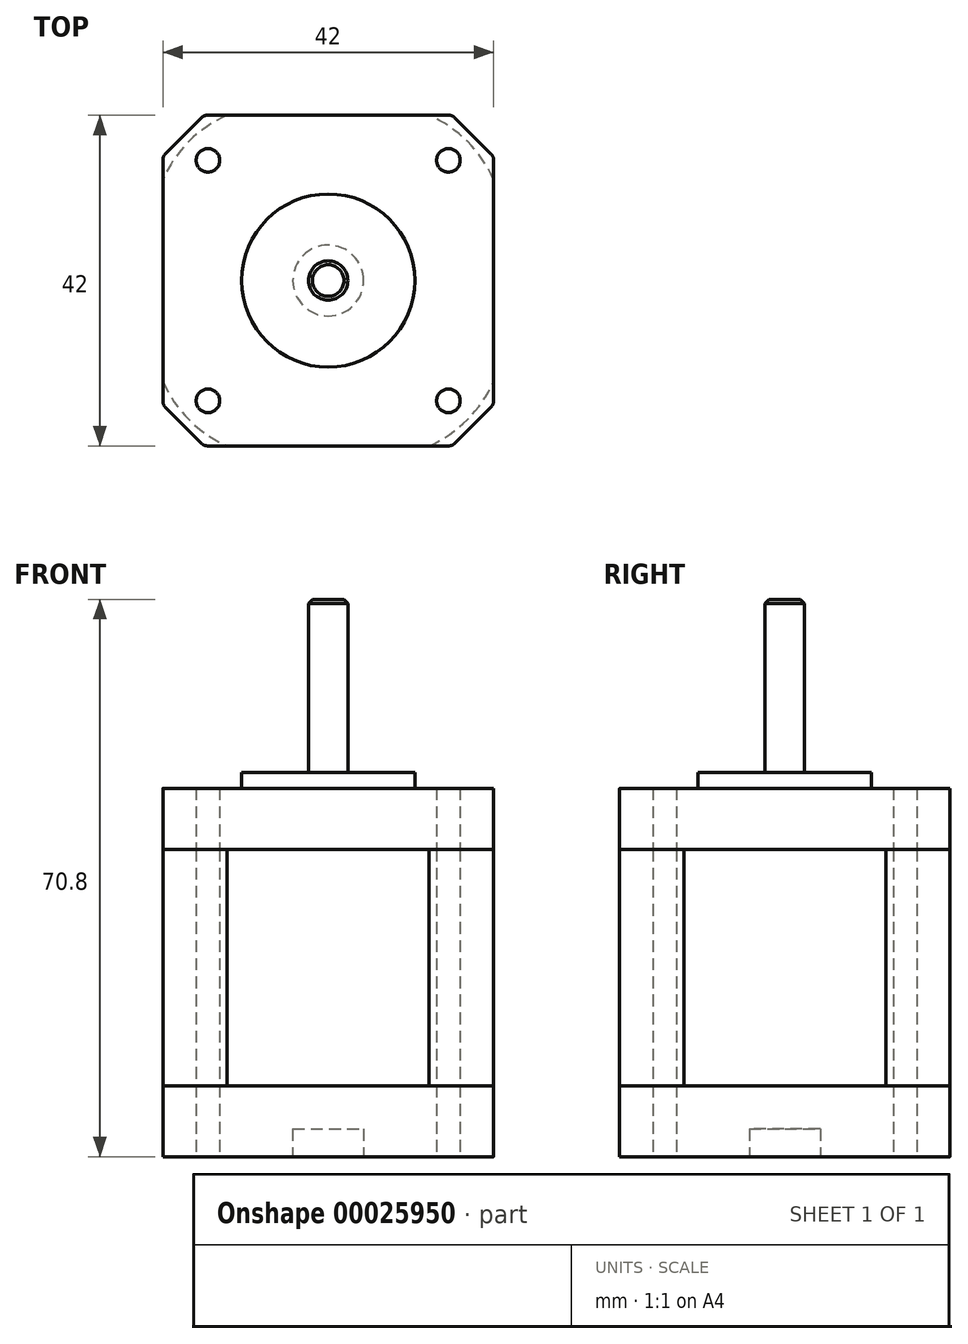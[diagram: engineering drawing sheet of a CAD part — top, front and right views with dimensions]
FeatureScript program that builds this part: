
annotation { "Feature Type Name" : "Feature", "Feature Type Description" : "" }
export const myFeature = defineFeature(function(context is Context, id is Id, definition is map)
    precondition{}
    {
        {
            var Q0;
            Q0=qCreatedBy(makeId("Top.planeOp"),FACE);
            var sketch = newSketch(context, id + "F0", { "sketchPlane" : qUnion([Q0])});
            skLineSegment(sketch, "E0.rect.bottom", {"start": v(-15.36, 21) * mm, "end": v(15.36, 21) * mm});
            skLineSegment(sketch, "E0.rect.top", {"start": v(-15.36, -21) * mm, "end": v(15.36, -21) * mm});
            skLineSegment(sketch, "E0.rect.left", {"start": v(-21, 15.36) * mm, "end": v(-21, -15.36) * mm});
            skLineSegment(sketch, "E0.rect.right", {"start": v(21, 15.36) * mm, "end": v(21, -15.36) * mm});
            skPoint(sketch, "E0.rect.middle", {"position": v(0, 0) * mm});
            skLineSegment(sketch, "E1", {"start": v(-20.7, 16.06) * mm, "end": v(-16.06, 20.7) * mm});
            skPoint(sketch, "E2.newPointA", {"position": v(-21, 21) * mm});
            skArc(sketch, "E2.filletArc", {"start": v(-20.7, 16.06) * mm, "mid": v(-20.92, 15.74) * mm, "end": v(-21, 15.36) * mm});
            skArc(sketch, "E3.filletArc", {"start": v(-15.36, 21) * mm, "mid": v(-15.74, 20.92) * mm, "end": v(-16.06, 20.7) * mm});
            skArc(sketch, "E4.1.0", {"start": v(-16.06, -20.7) * mm, "mid": v(-15.74, -20.92) * mm, "end": v(-15.36, -21) * mm});
            skLineSegment(sketch, "E4.1.1", {"start": v(-16.06, -20.7) * mm, "end": v(-20.7, -16.06) * mm});
            skArc(sketch, "E4.1.2", {"start": v(-21, -15.36) * mm, "mid": v(-20.92, -15.74) * mm, "end": v(-20.7, -16.06) * mm});
            skArc(sketch, "E4.2.0", {"start": v(20.7, -16.06) * mm, "mid": v(20.92, -15.74) * mm, "end": v(21, -15.36) * mm});
            skLineSegment(sketch, "E4.2.1", {"start": v(20.7, -16.06) * mm, "end": v(16.06, -20.7) * mm});
            skArc(sketch, "E4.2.2", {"start": v(15.36, -21) * mm, "mid": v(15.74, -20.92) * mm, "end": v(16.06, -20.7) * mm});
            skArc(sketch, "E4.3.0", {"start": v(16.06, 20.7) * mm, "mid": v(15.74, 20.92) * mm, "end": v(15.36, 21) * mm});
            skLineSegment(sketch, "E4.3.1", {"start": v(16.06, 20.7) * mm, "end": v(20.7, 16.06) * mm});
            skArc(sketch, "E4.3.2", {"start": v(21, 15.36) * mm, "mid": v(20.92, 15.74) * mm, "end": v(20.7, 16.06) * mm});
            skPoint(sketch, "E5.orphan", {"position": v(21, 21) * mm});
            skPoint(sketch, "E6.orphan", {"position": v(21, -21) * mm});
            skPoint(sketch, "E7.orphan", {"position": v(-21, -21) * mm});
            skSolve(sketch);
        }
        {
            var Q0;
            Q0=makeQuery(id+"F0.imprint","IMPRINT",FACE,{"disambiguationData":[TD([[makeQuery(id+"F0.imprint","IMPRINT",EDGE,{"derivedFrom":sQuery(id+"F0.wireOp",EDGE,"E0.rect.bottom")}),-1.0]])]});
            extrude(context, id + "F1", {"entities" : qUnion([Q0]), "depth" : 9 * mm});
        }
        {
            var Q0;
            Q0=makeQuery(id+"F1.opExtrude","CAP_FACE",FACE,{"disambiguationData":[OSD([sQuery(id+"F0.wireOp",EDGE,"E0.rect.bottom"),sQuery(id+"F0.wireOp",EDGE,"E0.rect.top"),sQuery(id+"F0.wireOp",EDGE,"E0.rect.left"),sQuery(id+"F0.wireOp",EDGE,"E0.rect.right"),sQuery(id+"F0.wireOp",EDGE,"E1"),sQuery(id+"F0.wireOp",EDGE,"E2.filletArc"),sQuery(id+"F0.wireOp",EDGE,"E3.filletArc"),sQuery(id+"F0.wireOp",EDGE,"E4.1.0"),sQuery(id+"F0.wireOp",EDGE,"E4.1.1"),sQuery(id+"F0.wireOp",EDGE,"E4.1.2"),sQuery(id+"F0.wireOp",EDGE,"E4.2.0"),sQuery(id+"F0.wireOp",EDGE,"E4.2.1"),sQuery(id+"F0.wireOp",EDGE,"E4.2.2"),sQuery(id+"F0.wireOp",EDGE,"E4.3.0"),sQuery(id+"F0.wireOp",EDGE,"E4.3.1"),sQuery(id+"F0.wireOp",EDGE,"E4.3.2")])],"isStart":false});
            var sketch = newSketch(context, id + "F2", { "sketchPlane" : qUnion([Q0])});
            skLineSegment(sketch, "E8.rect.bottom", {"start": v(-12.82, 21) * mm, "end": v(12.82, 21) * mm});
            skLineSegment(sketch, "E8.rect.top", {"start": v(-12.82, -21) * mm, "end": v(12.82, -21) * mm});
            skLineSegment(sketch, "E8.rect.left", {"start": v(-21, 12.82) * mm, "end": v(-21, -12.82) * mm});
            skLineSegment(sketch, "E8.rect.right", {"start": v(21, 12.82) * mm, "end": v(21, -12.82) * mm});
            skPoint(sketch, "E8.rect.middle", {"position": v(0, 0) * mm});
            skArc(sketch, "E9", {"start": v(-12.82, 21) * mm, "mid": v(-17.68, 17.68) * mm, "end": v(-21, 12.82) * mm});
            skPoint(sketch, "E10.orphan", {"position": v(-21, 0) * mm});
            skArc(sketch, "E11.1.0", {"start": v(-21, -12.82) * mm, "mid": v(-17.68, -17.68) * mm, "end": v(-12.82, -21) * mm});
            skArc(sketch, "E11.2.0", {"start": v(12.82, -21) * mm, "mid": v(17.68, -17.68) * mm, "end": v(21, -12.82) * mm});
            skArc(sketch, "E11.3.0", {"start": v(21, 12.82) * mm, "mid": v(17.68, 17.68) * mm, "end": v(12.82, 21) * mm});
            skPoint(sketch, "E12.orphan", {"position": v(-21, 21) * mm});
            skPoint(sketch, "E13.orphan", {"position": v(21, 21) * mm});
            skPoint(sketch, "E14.orphan", {"position": v(21, -21) * mm});
            skPoint(sketch, "E15.orphan", {"position": v(-21, -21) * mm});
            skSolve(sketch);
        }
        {
            var Q0;
            {var subQ3=sQuery(id+"F2.wireOp",EDGE,"E9");Q0=makeQuery(id+"F2.imprint","IMPRINT",FACE,{"disambiguationData":[TD([[makeQuery(id+"F2.imprint","IMPRINT",EDGE,{"derivedFrom":subQ3}),1.0]])]});}
            extrude(context, id + "F3", {"entities" : qUnion([Q0]), "depth" : 30 * mm});
        }
        {
            var Q0;
            Q0=makeQuery(id+"F3.opExtrude","CAP_FACE",FACE,{"disambiguationData":[OSD([sQuery(id+"F2.wireOp",EDGE,"E8.rect.bottom"),sQuery(id+"F2.wireOp",EDGE,"E8.rect.top"),sQuery(id+"F2.wireOp",EDGE,"E8.rect.left"),sQuery(id+"F2.wireOp",EDGE,"E8.rect.right"),sQuery(id+"F2.wireOp",EDGE,"E9"),sQuery(id+"F2.wireOp",EDGE,"E11.1.0"),sQuery(id+"F2.wireOp",EDGE,"E11.2.0"),sQuery(id+"F2.wireOp",EDGE,"E11.3.0")])],"isStart":false});
            var sketch = newSketch(context, id + "F4", { "sketchPlane" : qUnion([Q0])});
            skLineSegment(sketch, "E16.rect.bottom", {"start": v(-15.36, 21) * mm, "end": v(15.36, 21) * mm});
            skLineSegment(sketch, "E16.rect.top", {"start": v(-15.36, -21) * mm, "end": v(15.36, -21) * mm});
            skLineSegment(sketch, "E16.rect.left", {"start": v(-21, 15.36) * mm, "end": v(-21, -15.36) * mm});
            skLineSegment(sketch, "E16.rect.right", {"start": v(21, 15.36) * mm, "end": v(21, -15.36) * mm});
            skPoint(sketch, "E16.rect.middle", {"position": v(0, 0) * mm});
            skLineSegment(sketch, "E17", {"start": v(-20.7, 16.06) * mm, "end": v(-16.06, 20.7) * mm});
            skPoint(sketch, "E18.newPointA", {"position": v(-21, 37.25) * mm});
            skArc(sketch, "E18.filletArc", {"start": v(-20.7, 16.06) * mm, "mid": v(-20.92, 15.74) * mm, "end": v(-21, 15.36) * mm});
            skPoint(sketch, "E19.newPointA", {"position": v(-21, 21) * mm});
            skArc(sketch, "E19.filletArc", {"start": v(-15.36, 21) * mm, "mid": v(-15.74, 20.92) * mm, "end": v(-16.06, 20.7) * mm});
            skArc(sketch, "E20.1.0", {"start": v(-16.06, -20.7) * mm, "mid": v(-15.74, -20.92) * mm, "end": v(-15.36, -21) * mm});
            skLineSegment(sketch, "E20.1.1", {"start": v(-16.06, -20.7) * mm, "end": v(-20.7, -16.06) * mm});
            skArc(sketch, "E20.1.2", {"start": v(-21, -15.36) * mm, "mid": v(-20.92, -15.74) * mm, "end": v(-20.7, -16.06) * mm});
            skArc(sketch, "E20.2.0", {"start": v(20.7, -16.06) * mm, "mid": v(20.92, -15.74) * mm, "end": v(21, -15.36) * mm});
            skLineSegment(sketch, "E20.2.1", {"start": v(20.7, -16.06) * mm, "end": v(16.06, -20.7) * mm});
            skArc(sketch, "E20.2.2", {"start": v(15.36, -21) * mm, "mid": v(15.74, -20.92) * mm, "end": v(16.06, -20.7) * mm});
            skArc(sketch, "E20.3.0", {"start": v(16.06, 20.7) * mm, "mid": v(15.74, 20.92) * mm, "end": v(15.36, 21) * mm});
            skLineSegment(sketch, "E20.3.1", {"start": v(16.06, 20.7) * mm, "end": v(20.7, 16.06) * mm});
            skArc(sketch, "E20.3.2", {"start": v(21, 15.36) * mm, "mid": v(20.92, 15.74) * mm, "end": v(20.7, 16.06) * mm});
            skPoint(sketch, "E21.orphan", {"position": v(21, 21) * mm});
            skPoint(sketch, "E22.orphan", {"position": v(21, -21) * mm});
            skPoint(sketch, "E23.orphan", {"position": v(-21, -21) * mm});
            skSolve(sketch);
        }
        {
            var Q0;
            Q0 = qSketchRegion(id + "F4", true);
            extrude(context, id + "F5", {"entities" : qUnion([Q0]), "depth" : 7.8 * mm});
        }
        {
            var Q0;
            Q0=makeQuery(id+"F5.opExtrude","CAP_FACE",FACE,{"disambiguationData":[OSD([sQuery(id+"F4.wireOp",EDGE,"E16.rect.bottom"),sQuery(id+"F4.wireOp",EDGE,"E16.rect.top"),sQuery(id+"F4.wireOp",EDGE,"E16.rect.left"),sQuery(id+"F4.wireOp",EDGE,"E16.rect.right"),sQuery(id+"F4.wireOp",EDGE,"E17"),sQuery(id+"F4.wireOp",EDGE,"E18.filletArc"),sQuery(id+"F4.wireOp",EDGE,"E19.filletArc"),sQuery(id+"F4.wireOp",EDGE,"E20.1.0"),sQuery(id+"F4.wireOp",EDGE,"E20.1.1"),sQuery(id+"F4.wireOp",EDGE,"E20.1.2"),sQuery(id+"F4.wireOp",EDGE,"E20.2.0"),sQuery(id+"F4.wireOp",EDGE,"E20.2.1"),sQuery(id+"F4.wireOp",EDGE,"E20.2.2"),sQuery(id+"F4.wireOp",EDGE,"E20.3.0"),sQuery(id+"F4.wireOp",EDGE,"E20.3.1"),sQuery(id+"F4.wireOp",EDGE,"E20.3.2")])],"isStart":false});
            var sketch = newSketch(context, id + "F6", { "sketchPlane" : qUnion([Q0])});
            skCircle(sketch, "E24", {"center": v(0, 0) * mm, "radius": 11 * mm});
            skSolve(sketch);
        }
        {
            var Q0;
            Q0=makeQuery(id+"F6.imprint","IMPRINT",FACE,{"disambiguationData":[TD([[makeQuery(id+"F6.imprint","IMPRINT",EDGE,{"derivedFrom":sQuery(id+"F6.wireOp",EDGE,"E24")}),1.0]])]});
            extrude(context, id + "F7", {"entities" : qUnion([Q0]), "operationType" : NewBodyOperationType.ADD, "depth" : 2 * mm});
        }
        {
            var Q0;
            Q0=makeQuery(id+"F7.opExtrude","CAP_FACE",FACE,{"disambiguationData":[OSD([sQuery(id+"F6.wireOp",EDGE,"E24")])],"isStart":false});
            var sketch = newSketch(context, id + "F8", { "sketchPlane" : qUnion([Q0])});
            skCircle(sketch, "E25", {"center": v(0, 0) * mm, "radius": 2.5 * mm});
            skSolve(sketch);
        }
        {
            var Q0;
            Q0=makeQuery(id+"F8.imprint","IMPRINT",FACE,{"disambiguationData":[TD([[makeQuery(id+"F8.imprint","IMPRINT",EDGE,{"derivedFrom":sQuery(id+"F8.wireOp",EDGE,"E25")}),1.0]])]});
            extrude(context, id + "F9", {"entities" : qUnion([Q0]), "depth" : 22 * mm});
        }
        {
            var Q0;
            Q0=makeQuery(id+"F9.opExtrude","CAP_EDGE",EDGE,{"disambiguationData":[OSD([sQuery(id+"F8.wireOp",EDGE,"E25")])],"isStart":false});
            chamfer(context, id + "F10", {"entities" : qUnion([Q0]), "width" : .5 * mm, "tangentPropagation" : true});
        }
        {
            var Q0;
            Q0=makeQuery(id+"F5.opExtrude","CAP_FACE",FACE,{"disambiguationData":[OSD([sQuery(id+"F4.wireOp",EDGE,"E16.rect.bottom"),sQuery(id+"F4.wireOp",EDGE,"E16.rect.top"),sQuery(id+"F4.wireOp",EDGE,"E16.rect.left"),sQuery(id+"F4.wireOp",EDGE,"E16.rect.right"),sQuery(id+"F4.wireOp",EDGE,"E17"),sQuery(id+"F4.wireOp",EDGE,"E18.filletArc"),sQuery(id+"F4.wireOp",EDGE,"E19.filletArc"),sQuery(id+"F4.wireOp",EDGE,"E20.1.0"),sQuery(id+"F4.wireOp",EDGE,"E20.1.1"),sQuery(id+"F4.wireOp",EDGE,"E20.1.2"),sQuery(id+"F4.wireOp",EDGE,"E20.2.0"),sQuery(id+"F4.wireOp",EDGE,"E20.2.1"),sQuery(id+"F4.wireOp",EDGE,"E20.2.2"),sQuery(id+"F4.wireOp",EDGE,"E20.3.0"),sQuery(id+"F4.wireOp",EDGE,"E20.3.1"),sQuery(id+"F4.wireOp",EDGE,"E20.3.2")])],"isStart":false});
            var sketch = newSketch(context, id + "F11", { "sketchPlane" : qUnion([Q0])});
            skPoint(sketch, "E26", {"position": v(-15.27, -15.27) * mm});
            skLineSegment(sketch, "E27", {"start": v(0, 0) * mm, "end": v(-15.27, -15.27) * mm, "construction": true});
            skLineSegment(sketch, "E28", {"start": v(0, 0) * mm, "end": v(0, -21) * mm, "construction": true});
            skPoint(sketch, "E29.1.0", {"position": v(15.27, -15.27) * mm});
            skPoint(sketch, "E29.2.0", {"position": v(15.27, 15.27) * mm});
            skPoint(sketch, "E29.3.0", {"position": v(-15.27, 15.27) * mm});
            skPoint(sketch, "E29.center", {"position": v(0, 0) * mm});
            skSolve(sketch);
        }
        {
            var Q0;
            Q0=sQuery(id+"F11.wireOp",VERTEX,"E29.2.0");
            var Q1;
            Q1=sQuery(id+"F11.wireOp",VERTEX,"E29.1.0");
            var Q2;
            Q2=sQuery(id+"F11.wireOp",VERTEX,"E26");
            var Q3;
            Q3=sQuery(id+"F11.wireOp",VERTEX,"E29.3.0");
            var Q4;
            Q4=makeQuery(id+"F5.opExtrude","SWEPT_BODY",BODY,{"disambiguationData":[OSD([sQuery(id+"F4.wireOp",EDGE,"E16.rect.bottom"),sQuery(id+"F4.wireOp",EDGE,"E16.rect.top"),sQuery(id+"F4.wireOp",EDGE,"E16.rect.left"),sQuery(id+"F4.wireOp",EDGE,"E16.rect.right"),sQuery(id+"F4.wireOp",EDGE,"E17"),sQuery(id+"F4.wireOp",EDGE,"E18.filletArc"),sQuery(id+"F4.wireOp",EDGE,"E19.filletArc"),sQuery(id+"F4.wireOp",EDGE,"E20.1.0"),sQuery(id+"F4.wireOp",EDGE,"E20.1.1"),sQuery(id+"F4.wireOp",EDGE,"E20.1.2"),sQuery(id+"F4.wireOp",EDGE,"E20.2.0"),sQuery(id+"F4.wireOp",EDGE,"E20.2.1"),sQuery(id+"F4.wireOp",EDGE,"E20.2.2"),sQuery(id+"F4.wireOp",EDGE,"E20.3.0"),sQuery(id+"F4.wireOp",EDGE,"E20.3.1"),sQuery(id+"F4.wireOp",EDGE,"E20.3.2")])]});
            var Q5;
            Q5=makeQuery(id+"F3.opExtrude","SWEPT_BODY",BODY,{"disambiguationData":[OSD([sQuery(id+"F2.wireOp",EDGE,"E8.rect.bottom"),sQuery(id+"F2.wireOp",EDGE,"E8.rect.top"),sQuery(id+"F2.wireOp",EDGE,"E8.rect.left"),sQuery(id+"F2.wireOp",EDGE,"E8.rect.right"),sQuery(id+"F2.wireOp",EDGE,"E9"),sQuery(id+"F2.wireOp",EDGE,"E11.1.0"),sQuery(id+"F2.wireOp",EDGE,"E11.2.0"),sQuery(id+"F2.wireOp",EDGE,"E11.3.0")])]});
            var Q6;
            Q6=makeQuery(id+"F1.opExtrude","SWEPT_BODY",BODY,{"disambiguationData":[OSD([sQuery(id+"F0.wireOp",EDGE,"E0.rect.bottom"),sQuery(id+"F0.wireOp",EDGE,"E0.rect.top"),sQuery(id+"F0.wireOp",EDGE,"E0.rect.left"),sQuery(id+"F0.wireOp",EDGE,"E0.rect.right"),sQuery(id+"F0.wireOp",EDGE,"E1"),sQuery(id+"F0.wireOp",EDGE,"E2.filletArc"),sQuery(id+"F0.wireOp",EDGE,"E3.filletArc"),sQuery(id+"F0.wireOp",EDGE,"E4.1.0"),sQuery(id+"F0.wireOp",EDGE,"E4.1.1"),sQuery(id+"F0.wireOp",EDGE,"E4.1.2"),sQuery(id+"F0.wireOp",EDGE,"E4.2.0"),sQuery(id+"F0.wireOp",EDGE,"E4.2.1"),sQuery(id+"F0.wireOp",EDGE,"E4.2.2"),sQuery(id+"F0.wireOp",EDGE,"E4.3.0"),sQuery(id+"F0.wireOp",EDGE,"E4.3.1"),sQuery(id+"F0.wireOp",EDGE,"E4.3.2")])]});
            hole(context, id + "F12", {"style" : HoleStyle.SIMPLE, "holeDiameter" : 3 * mm, "endStyle" : HoleEndStyle.THROUGH, "locations" : qUnion([Q0, Q1, Q2, Q3]), "scope" : qUnion([Q4, Q5, Q6])});
        }
        {
            var Q0;
            Q0=makeQuery(id+"F1.opExtrude","CAP_FACE",FACE,{"disambiguationData":[OSD([sQuery(id+"F0.wireOp",EDGE,"E0.rect.bottom"),sQuery(id+"F0.wireOp",EDGE,"E0.rect.top"),sQuery(id+"F0.wireOp",EDGE,"E0.rect.left"),sQuery(id+"F0.wireOp",EDGE,"E0.rect.right"),sQuery(id+"F0.wireOp",EDGE,"E1"),sQuery(id+"F0.wireOp",EDGE,"E2.filletArc"),sQuery(id+"F0.wireOp",EDGE,"E3.filletArc"),sQuery(id+"F0.wireOp",EDGE,"E4.1.0"),sQuery(id+"F0.wireOp",EDGE,"E4.1.1"),sQuery(id+"F0.wireOp",EDGE,"E4.1.2"),sQuery(id+"F0.wireOp",EDGE,"E4.2.0"),sQuery(id+"F0.wireOp",EDGE,"E4.2.1"),sQuery(id+"F0.wireOp",EDGE,"E4.2.2"),sQuery(id+"F0.wireOp",EDGE,"E4.3.0"),sQuery(id+"F0.wireOp",EDGE,"E4.3.1"),sQuery(id+"F0.wireOp",EDGE,"E4.3.2")])],"isStart":true});
            var sketch = newSketch(context, id + "F13", { "sketchPlane" : qUnion([Q0])});
            skCircle(sketch, "E30", {"center": v(0, 0) * mm, "radius": 4.5 * mm});
            skSolve(sketch);
        }
        {
            var Q0;
            Q0=makeQuery(id+"F13.imprint","IMPRINT",FACE,{"disambiguationData":[TD([[makeQuery(id+"F13.imprint","IMPRINT",EDGE,{"derivedFrom":sQuery(id+"F13.wireOp",EDGE,"E30")}),1.0]])]});
            extrude(context, id + "F14", {"entities" : qUnion([Q0]), "operationType" : NewBodyOperationType.REMOVE, "oppositeDirection" : true, "depth" : 3.5 * mm});
        }
    });
